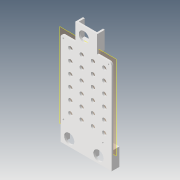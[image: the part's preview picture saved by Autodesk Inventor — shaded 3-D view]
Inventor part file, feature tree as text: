
AUTODESK INVENTOR PART (.ipt)
format: ipt  version: 2022 (Build 260153000, 153)  size: 275,968 bytes
history: native  units: mm
features: reference x11, other x7, extrude x4, sketch x4, plane x2, pattern_linear x1, projected_geometry x1
ambient origin geometry x8: Origin, YZ Plane, XZ Plane, XY Plane, X Axis, Y Axis, Z Axis, Center Point
bodies: Volumenkörper1 (feature_tree)
feature tree (30):
  plane  "Arbeitsebene1"
  extrude  "Extrusion1"  Depth=3.0mm
  extrude  "Extrusion2"  Depth=60.0mm
  pattern_linear  "Rechteckige Anordnung1"  Count1=4 Spacing1=18.9mm
  sketch  "Skizze3"  dims[d11=2.0mm d12=0.0mm d13=3.0mm]
  plane  "Arbeitsebene2"
  extrude  "Extrusion3"  Depth=3.0mm
  extrude  "Extrusion4"  Depth=10.0mm TaperAngle=0.0deg
  sketch  "Skizze1"  dims[d0=3.0mm d1=0.0mm d2=7.0mm]
  reference  "Referenz1"
  sketch  "Skizze2"  dims[d3=0.0mm d4=0.0mm d5=60.0mm d7=18.9mm d8=40.0mm d10=18.9mm]
  reference  "Referenz2"
  reference  "Referenz3"
  reference  "Referenz4"
  reference  "Referenz5"
  projected_geometry  "Projizierte Kontur1"
  sketch  "Skizze4"  dims[d14=3.0mm d15=10.0mm d16=0.0mm d17=3.0mm d18=3.0mm]
  reference  "Referenz6"
  reference  "Referenz7"
  reference  "Referenz8"
  reference  "Referenz9"
  reference  "Referenz10"
  reference  "Referenz11"
  other  "Omniscope_new_v0.iam"
  other  "Omniscope_sidewalls_v0:1"
  other  "OV_Camera:1"
  other  "00_Z_Focus_CCTV_Camera:1"
  other  "00_Z_Focus_CCTV_Camera:3"
  other  "00_Z_Focus_CCTV_Camera:2"
  other  "Omniscope_sidewall_spacer_v0:1"
